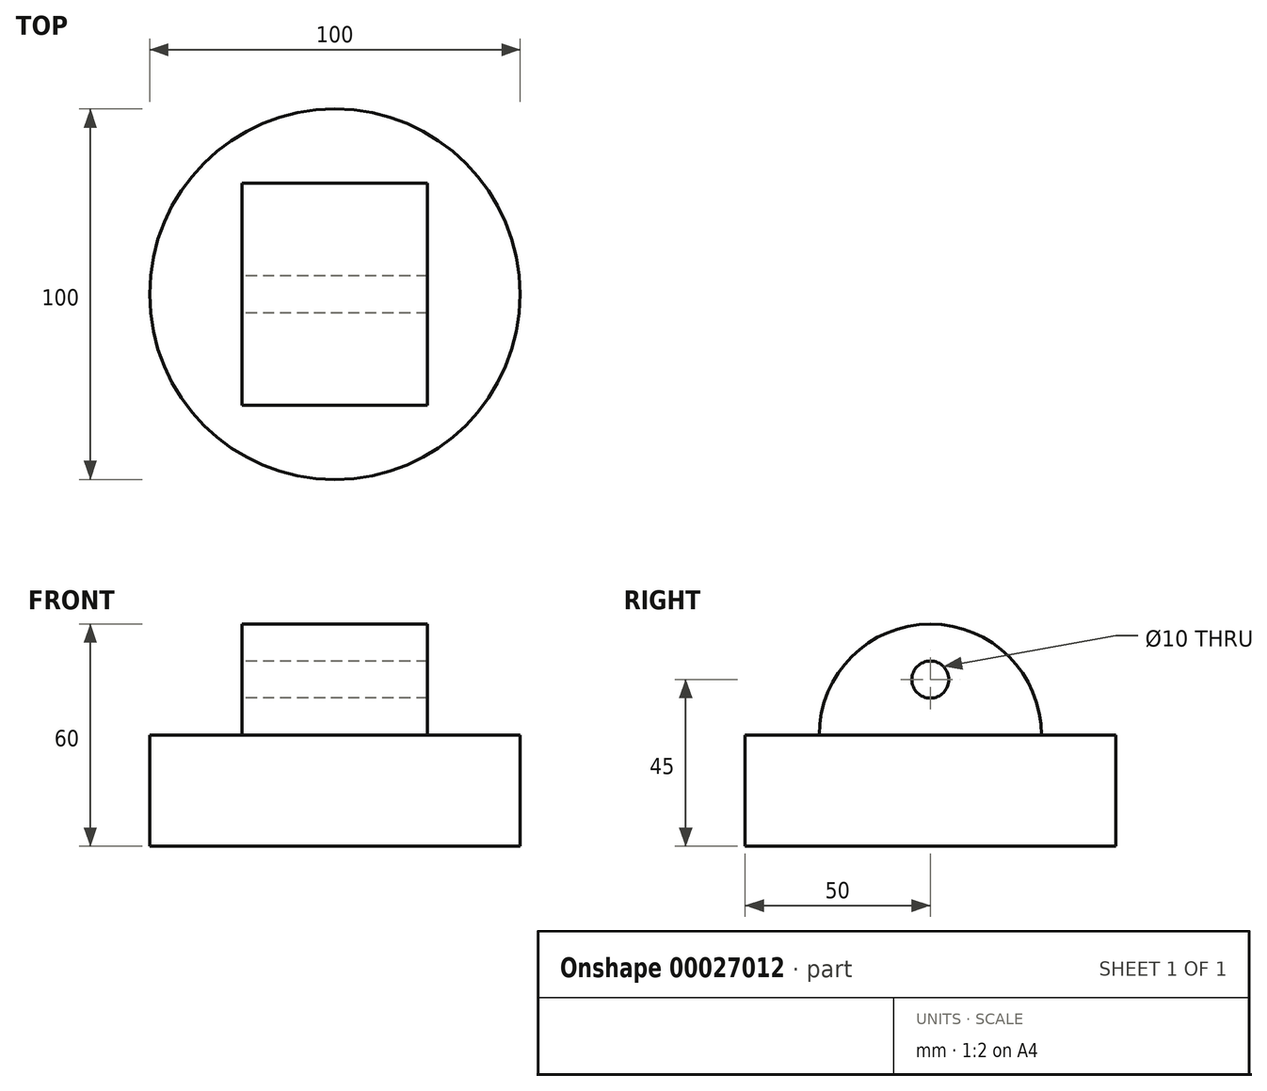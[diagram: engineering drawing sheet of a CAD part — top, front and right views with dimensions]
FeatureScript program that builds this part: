
annotation { "Feature Type Name" : "Feature", "Feature Type Description" : "" }
export const myFeature = defineFeature(function(context is Context, id is Id, definition is map)
    precondition{}
    {
        {
            var Q0;
            Q0=qCreatedBy(makeId("Top.planeOp"),FACE);
            var sketch = newSketch(context, id + "F0", { "sketchPlane" : qUnion([Q0])});
            skCircle(sketch, "E0", {"center": v(0, 0) * mm, "radius": 50 * mm});
            skSolve(sketch);
        }
        {
            var Q0;
            Q0=makeQuery(id+"F0.imprint","IMPRINT",FACE,{"disambiguationData":[TD([[makeQuery(id+"F0.imprint","IMPRINT",EDGE,{"derivedFrom":sQuery(id+"F0.wireOp",EDGE,"E0")}),1.0]])]});
            extrude(context, id + "F1", {"entities" : qUnion([Q0]), "depth" : 30 * mm});
        }
        {
            var Q0;
            Q0=qCreatedBy(makeId("Right.planeOp"),FACE);
            var sketch = newSketch(context, id + "F2", { "sketchPlane" : qUnion([Q0])});
            skCircle(sketch, "E1", {"center": v(0, 30) * mm, "radius": 30 * mm});
            skCircle(sketch, "E2", {"center": v(0, 45) * mm, "radius": 5 * mm});
            skSolve(sketch);
        }
        {
            var Q0;
            Q0=makeQuery(id+"F2.imprint","IMPRINT",FACE,{"disambiguationData":[TD([[makeQuery(id+"F2.imprint","IMPRINT",EDGE,{"derivedFrom":sQuery(id+"F2.wireOp",EDGE,"E1")}),1.0]])]});
            extrude(context, id + "F3", {"entities" : qUnion([Q0]), "operationType" : NewBodyOperationType.ADD, "depth" : 25 * mm, "hasSecondDirection" : true, "secondDirectionOppositeDirection" : true, "secondDirectionDepth" : 25 * mm});
        }
    });
